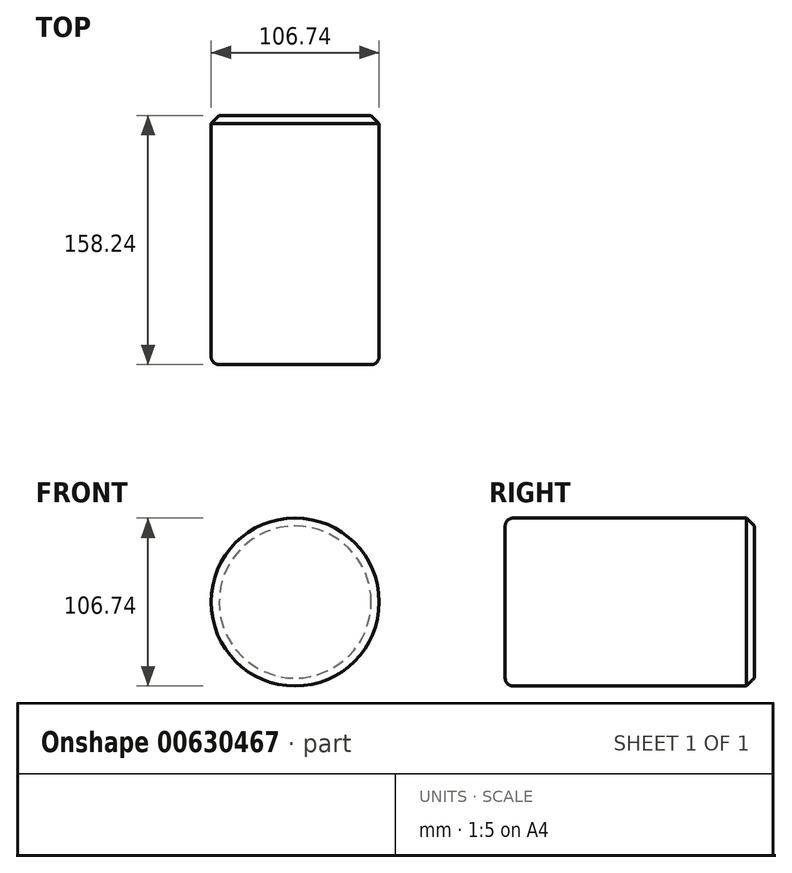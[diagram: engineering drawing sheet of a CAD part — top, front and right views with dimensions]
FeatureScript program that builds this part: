
annotation { "Feature Type Name" : "Feature", "Feature Type Description" : "" }
export const myFeature = defineFeature(function(context is Context, id is Id, definition is map)
    precondition{}
    {
        {
            var Q0;
            Q0=qCreatedBy(makeId("Front.planeOp"),FACE);
            var sketch = newSketch(context, id + "F0", { "sketchPlane" : qUnion([Q0])});
            skCircle(sketch, "E0", {"center": v(0, 0) * mm, "radius": 53.37 * mm});
            skSolve(sketch);
        }
        {
            var Q0;
            Q0 = qSketchRegion(id + "F0", true);
            extrude(context, id + "F1", {"entities" : qUnion([Q0]), "depth" : 158.24 * mm, "offsetDistance" : 25.4 * mm});
        }
        {
            var Q0;
            Q0=makeQuery(id+"F1.opExtrude","CAP_EDGE",EDGE,{"disambiguationData":[OSD([sQuery(id+"F0.wireOp",EDGE,"E0")])],"isStart":false});
            fillet(context, id + "F2", {"entities" : qUnion([Q0]), "radius" : 5.08 * mm, "tangentPropagation" : true, "allowEdgeOverflow" : false});
        }
        {
            var Q0;
            Q0=makeQuery(id+"F1.opExtrude","CAP_EDGE",EDGE,{"disambiguationData":[OSD([sQuery(id+"F0.wireOp",EDGE,"E0")])],"isStart":true});
            chamfer(context, id + "F3", {"entities" : qUnion([Q0]), "width" : 5.08 * mm, "tangentPropagation" : true});
        }
    });
